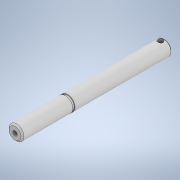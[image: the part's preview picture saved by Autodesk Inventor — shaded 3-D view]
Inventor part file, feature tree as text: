
AUTODESK INVENTOR PART (.ipt)
format: ipt  version: 2022 (Build 260153000, 153)  size: 138,240 bytes
history: native  units: mm
features: sketch x3, extrude x2, revolve x1, plane x1, thread x1
ambient origin geometry x8: Origin, YZ Plane, XZ Plane, XY Plane, X Axis, Y Axis, Z Axis, Center Point
bodies: Solid1 (feature_tree)
feature tree (8):
  revolve  "Revolution1"  [1 undecoded]
  plane  "Work Plane1"
  extrude  "Extrusion1"  Depth=0.5mm
  extrude  "Extrusion2"  Depth=10.0mm
  thread  "Thread1"  [1 undecoded]
  sketch  "Sketch1"  dims[d0=5.0mm d1=100.0mm]
  sketch  "Sketch2"  dims[d2=1.5mm d3=0.5mm]
  sketch  "Sketch3"  dims[d4=135.0deg d5=10.0mm d6=55.0mm d7=1.41mm d8=45.0deg d9=1.414214mm d10=90.0deg d11=3.5mm d12=3.0mm d13=10.0mm d14=0.0mm d15=3.0mm d16=10.0mm d17=0.0mm d18=10.0mm d19=0.0mm]
note: 2 required parameter values undecoded (feature->parameter linkage not recoverable at this tier; creation-order binding heuristic only, values carry confidence <= 0.55)